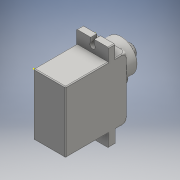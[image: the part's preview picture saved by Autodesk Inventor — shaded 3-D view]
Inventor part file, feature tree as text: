
AUTODESK INVENTOR PART (.ipt)
format: ipt  version: 2016 (Build 200138000, 138)  size: 399,360 bytes
history: native  units: mm
features: sketch x10, fillet x9, extrude x7
ambient origin geometry x8: Origin, YZ Plane, XZ Plane, XY Plane, X Axis, Y Axis, Z Axis, Center Point
bodies: 实体1 (feature_tree)
feature tree (26):
  sketch  "草图1"  dims[d0=22.7mm d1=22.7mm]
  extrude  "拉伸1"  Depth=22.7mm
  extrude  "拉伸2"  Depth=11.8mm
  extrude  "拉伸3"  Depth=4.7mm
  sketch  "草图5"  dims[d17=2.0mm d18=2.0mm]
  sketch  "草图6"  dims[d25=10.0mm d26=0.0mm d31=4.0mm d32=0.0mm]
  extrude  "拉伸4"  Depth=4.7mm
  sketch  "草图7"  dims[d34=4.6mm d35=3.2mm d36=0.0mm d37=1.7mm d38=7.2mm d39=0.0mm d40=0.2mm d41=0.3mm d42=0.3mm]
  sketch  "草图8"  dims[d43=2.0mm d44=2.0mm d45=2.0mm d46=2.0mm d47=2.0mm d48=2.0mm d49=2.0mm d50=2.0mm d51=2.0mm d52=2.0mm d53=2.0mm d54=2.0mm d55=0.3mm d56=0.3mm d57=0.3mm d58=0.3mm d59=0.3mm]
  extrude  "拉伸5"  Depth=2.0mm
  extrude  "拉伸6"  Depth=10.0mm TaperAngle=0.0deg
  extrude  "拉伸7"  Depth=0.3mm TaperAngle=0.0deg
  fillet  "圆角1"  Radius=1.7mm
  fillet  "圆角2"  Radius=7.2mm
  fillet  "圆角3"  Radius=0.2mm
  fillet  "圆角4"  Radius=0.3mm
  fillet  "圆角5"  Radius=0.3mm
  fillet  "圆角6"  Radius=0.3mm
  fillet  "圆角7"  Radius=0.3mm
  fillet  "圆角8"  Radius=0.3mm
  fillet  "圆角9"  Radius=0.3mm
  sketch  "草图2"  dims[d2=11.8mm d3=0.0mm d4=2.5mm]
  sketch  "草图3"  dims[d5=4.7mm d6=0.0mm d7=2.5mm]
  sketch  "草图4"  dims[d8=4.7mm d9=0.0mm d11=4.6mm]
  sketch  "草图9"  dims[d60=0.3mm]
  sketch  "草图10"
